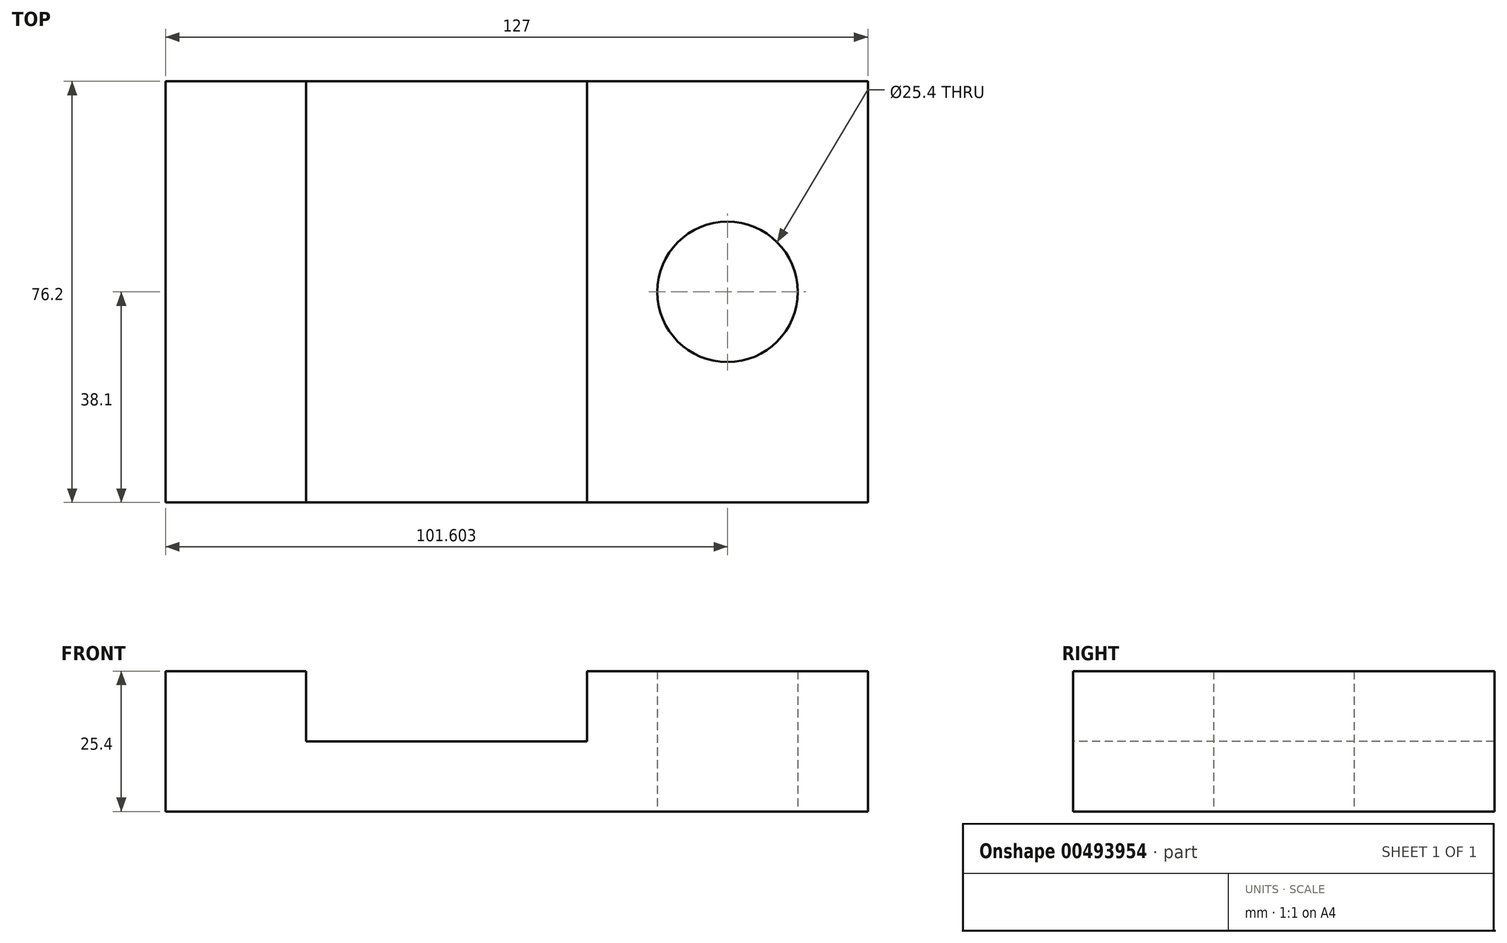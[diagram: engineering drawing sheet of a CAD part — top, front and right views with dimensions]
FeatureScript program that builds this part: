
annotation { "Feature Type Name" : "Feature", "Feature Type Description" : "" }
export const myFeature = defineFeature(function(context is Context, id is Id, definition is map)
    precondition{}
    {
        {
            var Q0;
            Q0=qCreatedBy(makeId("Front.planeOp"),FACE);
            var sketch = newSketch(context, id + "F0", { "sketchPlane" : qUnion([Q0])});
            skLineSegment(sketch, "E0.bottom", {"start": v(-38.72, 0) * mm, "end": v(88.28, 0) * mm});
            skLineSegment(sketch, "E0.top", {"start": v(-38.72, 25.4) * mm, "end": v(88.28, 25.4) * mm});
            skLineSegment(sketch, "E0.left", {"start": v(-38.72, 0) * mm, "end": v(-38.72, 25.4) * mm});
            skLineSegment(sketch, "E0.right", {"start": v(88.28, 0) * mm, "end": v(88.28, 25.4) * mm});
            skLineSegment(sketch, "E1", {"start": v(-13.32, 25.4) * mm, "end": v(-13.32, 12.7) * mm});
            skLineSegment(sketch, "E2", {"start": v(-13.32, 12.7) * mm, "end": v(37.48, 12.7) * mm});
            skLineSegment(sketch, "E3", {"start": v(37.48, 12.7) * mm, "end": v(37.48, 25.4) * mm});
            skLineSegment(sketch, "E4", {"start": v(37.48, 25.4) * mm, "end": v(-13.32, 25.4) * mm});
            skSolve(sketch);
        }
        {
            var Q0;
            Q0=makeQuery(id+"F0.imprint","IMPRINT",FACE,{"disambiguationData":[TD([[makeQuery(id+"F0.imprint","IMPRINT",EDGE,{"derivedFrom":sQuery(id+"F0.wireOp",EDGE,"E0.bottom")}),1.0]])]});
            extrude(context, id + "F1", {"entities" : qUnion([Q0]), "oppositeDirection" : true, "depth" : 76.2 * mm});
        }
        {
            var Q0;
            Q0=qCreatedBy(makeId("Top.planeOp"),FACE);
            var sketch = newSketch(context, id + "F2", { "sketchPlane" : qUnion([Q0])});
            skPoint(sketch, "E5", {"position": v(62.88, 38.1) * mm});
            skCircle(sketch, "E6", {"center": v(62.88, 38.1) * mm, "radius": 12.7 * mm});
            skSolve(sketch);
        }
        {
            var Q0;
            Q0=sQuery(id+"F2.wireOp",VERTEX,"E5");
            var Q1;
            Q1=makeQuery(id+"F1.opExtrude","SWEPT_BODY",BODY,{"disambiguationData":[OSD([sQuery(id+"F0.wireOp",EDGE,"E0.bottom"),sQuery(id+"F0.wireOp",EDGE,"E0.top"),sQuery(id+"F0.wireOp",EDGE,"E0.left"),sQuery(id+"F0.wireOp",EDGE,"E0.right"),sQuery(id+"F0.wireOp",EDGE,"E1"),sQuery(id+"F0.wireOp",EDGE,"E2"),sQuery(id+"F0.wireOp",EDGE,"E3")])]});
            hole(context, id + "F3", {"style" : HoleStyle.SIMPLE, "endStyle" : HoleEndStyle.THROUGH, "oppositeDirection" : true, "holeDiameter" : 25.4 * mm, "isTappedThrough" : true, "tappedDepth" : 12.7 * mm, "tapClearance" : 3, "locations" : qUnion([Q0]), "scope" : qUnion([Q1])});
        }
    });
